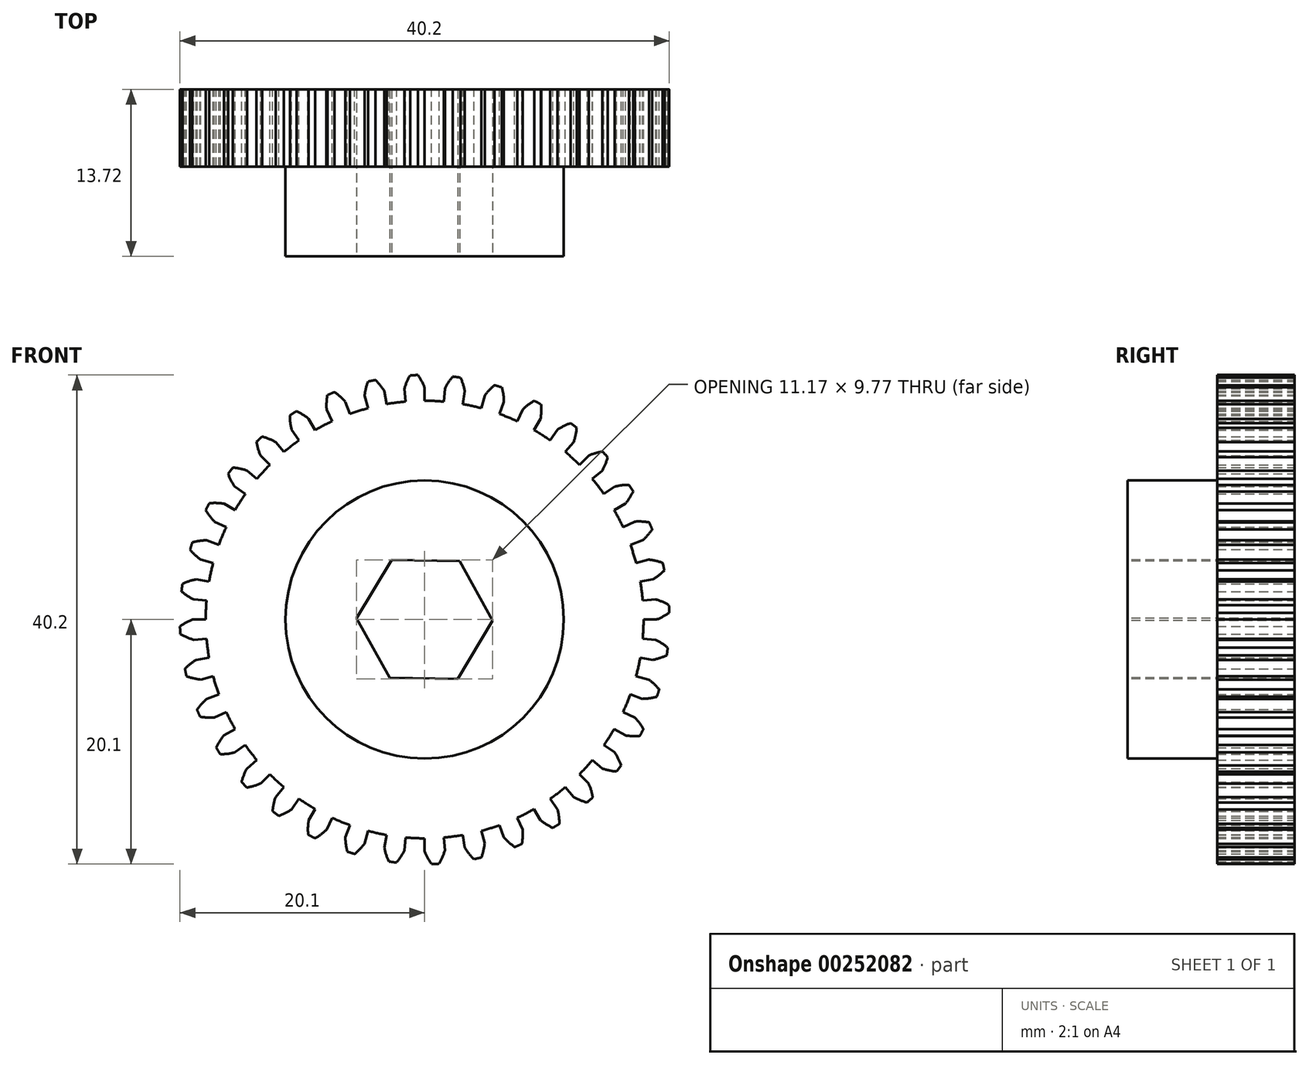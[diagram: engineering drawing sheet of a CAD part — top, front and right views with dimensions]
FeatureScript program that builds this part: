
annotation { "Feature Type Name" : "Feature", "Feature Type Description" : "" }
export const myFeature = defineFeature(function(context is Context, id is Id, definition is map)
    precondition{}
    {
        {
            var Q0;
            Q0=qCreatedBy(makeId("Front.planeOp"),FACE);
            var sketch = newSketch(context, id + "F0", { "sketchPlane" : qUnion([Q0])});
            skArc(sketch, "E0", {"start": v(-0.56, 20.1) * mm, "mid": v(-0.72, 20.1) * mm, "end": v(-0.88, 20.08) * mm});
            skArc(sketch, "E1", {"start": v(-14.73, 10.31) * mm, "mid": v(-15.17, 9.66) * mm, "end": v(-15.57, 9) * mm});
            skLineSegment(sketch, "E2", {"start": v(0, 17.98) * mm, "end": v(0, 19.05) * mm});
            skArc(sketch, "E3.trimOffspring", {"start": v(0, 19.05) * mm, "mid": v(-0.25, 19.6) * mm, "end": v(-0.56, 20.1) * mm});
            skPoint(sketch, "E4.orphan", {"position": v(-2.13, 48.9) * mm});
            skPoint(sketch, "E5.orphan", {"position": v(-2.13, 24.4) * mm});
            skArc(sketch, "E6.MirrorCS", {"start": v(-1.2, 20.07) * mm, "mid": v(-1.03, 20.08) * mm, "end": v(-0.88, 20.08) * mm});
            skArc(sketch, "E7.MirrorCS", {"start": v(-1.66, 18.98) * mm, "mid": v(-1.46, 19.54) * mm, "end": v(-1.2, 20.07) * mm});
            skLineSegment(sketch, "E8.MirrorCS", {"start": v(-1.57, 17.91) * mm, "end": v(-1.66, 18.98) * mm});
            skLineSegment(sketch, "E9.1.0", {"start": v(-4.65, 17.37) * mm, "end": v(-4.93, 18.4) * mm});
            skLineSegment(sketch, "E9.1.1", {"start": v(-3.12, 17.7) * mm, "end": v(-3.3, 18.76) * mm});
            skArc(sketch, "E9.1.2", {"start": v(-4.93, 18.4) * mm, "mid": v(-4.83, 18.99) * mm, "end": v(-4.66, 19.56) * mm});
            skArc(sketch, "E9.1.3", {"start": v(-3.3, 18.76) * mm, "mid": v(-3.65, 19.25) * mm, "end": v(-4.04, 19.7) * mm});
            skArc(sketch, "E9.1.4", {"start": v(-4.04, 19.7) * mm, "mid": v(-4.2, 19.66) * mm, "end": v(-4.35, 19.63) * mm});
            skArc(sketch, "E9.1.5", {"start": v(-4.66, 19.56) * mm, "mid": v(-4.5, 19.6) * mm, "end": v(-4.35, 19.63) * mm});
            skLineSegment(sketch, "E9.2.0", {"start": v(-7.6, 16.3) * mm, "end": v(-8.05, 17.27) * mm});
            skLineSegment(sketch, "E9.2.1", {"start": v(-6.15, 16.9) * mm, "end": v(-6.52, 17.9) * mm});
            skArc(sketch, "E9.2.2", {"start": v(-8.05, 17.27) * mm, "mid": v(-8.05, 17.86) * mm, "end": v(-7.98, 18.45) * mm});
            skArc(sketch, "E9.2.3", {"start": v(-6.52, 17.9) * mm, "mid": v(-6.93, 18.32) * mm, "end": v(-7.4, 18.7) * mm});
            skArc(sketch, "E9.2.4", {"start": v(-7.4, 18.7) * mm, "mid": v(-7.55, 18.63) * mm, "end": v(-7.7, 18.57) * mm});
            skArc(sketch, "E9.2.5", {"start": v(-7.98, 18.45) * mm, "mid": v(-7.84, 18.51) * mm, "end": v(-7.7, 18.57) * mm});
            skLineSegment(sketch, "E9.3.0", {"start": v(-10.31, 14.73) * mm, "end": v(-10.93, 15.6) * mm});
            skLineSegment(sketch, "E9.3.1", {"start": v(-9, 15.57) * mm, "end": v(-9.52, 16.5) * mm});
            skArc(sketch, "E9.3.2", {"start": v(-10.93, 15.6) * mm, "mid": v(-11.03, 16.19) * mm, "end": v(-11.07, 16.78) * mm});
            skArc(sketch, "E9.3.3", {"start": v(-9.52, 16.5) * mm, "mid": v(-10, 16.84) * mm, "end": v(-10.53, 17.12) * mm});
            skArc(sketch, "E9.3.4", {"start": v(-10.53, 17.12) * mm, "mid": v(-10.67, 17.04) * mm, "end": v(-10.8, 16.96) * mm});
            skArc(sketch, "E9.3.5", {"start": v(-11.07, 16.78) * mm, "mid": v(-10.93, 16.87) * mm, "end": v(-10.8, 16.96) * mm});
            skLineSegment(sketch, "E9.4.0", {"start": v(-12.72, 12.72) * mm, "end": v(-13.47, 13.47) * mm});
            skLineSegment(sketch, "E9.4.1", {"start": v(-11.56, 13.78) * mm, "end": v(-12.25, 14.6) * mm});
            skArc(sketch, "E9.4.2", {"start": v(-13.47, 13.47) * mm, "mid": v(-13.68, 14.03) * mm, "end": v(-13.81, 14.6) * mm});
            skArc(sketch, "E9.4.3", {"start": v(-12.25, 14.6) * mm, "mid": v(-12.78, 14.85) * mm, "end": v(-13.35, 15.03) * mm});
            skArc(sketch, "E9.4.4", {"start": v(-13.35, 15.03) * mm, "mid": v(-13.47, 14.93) * mm, "end": v(-13.58, 14.82) * mm});
            skArc(sketch, "E9.4.5", {"start": v(-13.81, 14.6) * mm, "mid": v(-13.7, 14.72) * mm, "end": v(-13.58, 14.82) * mm});
            skLineSegment(sketch, "E9.5.0", {"start": v(-14.73, 10.31) * mm, "end": v(-15.6, 10.93) * mm});
            skLineSegment(sketch, "E9.5.1", {"start": v(-13.78, 11.56) * mm, "end": v(-14.6, 12.25) * mm});
            skArc(sketch, "E9.5.2", {"start": v(-15.6, 10.93) * mm, "mid": v(-15.9, 11.44) * mm, "end": v(-16.14, 11.99) * mm});
            skArc(sketch, "E9.5.3", {"start": v(-14.6, 12.25) * mm, "mid": v(-15.17, 12.4) * mm, "end": v(-15.76, 12.49) * mm});
            skArc(sketch, "E9.5.4", {"start": v(-15.76, 12.49) * mm, "mid": v(-15.85, 12.36) * mm, "end": v(-15.95, 12.24) * mm});
            skArc(sketch, "E9.5.5", {"start": v(-16.14, 11.99) * mm, "mid": v(-16.05, 12.11) * mm, "end": v(-15.95, 12.24) * mm});
            skLineSegment(sketch, "E9.6.0", {"start": v(-16.3, 7.6) * mm, "end": v(-17.27, 8.05) * mm});
            skLineSegment(sketch, "E9.6.1", {"start": v(-15.57, 9) * mm, "end": v(-16.5, 9.53) * mm});
            skArc(sketch, "E9.6.2", {"start": v(-17.27, 8.05) * mm, "mid": v(-17.65, 8.5) * mm, "end": v(-17.98, 9) * mm});
            skArc(sketch, "E9.6.3", {"start": v(-16.5, 9.53) * mm, "mid": v(-17.09, 9.58) * mm, "end": v(-17.68, 9.56) * mm});
            skArc(sketch, "E9.6.4", {"start": v(-17.68, 9.56) * mm, "mid": v(-17.76, 9.42) * mm, "end": v(-17.83, 9.28) * mm});
            skArc(sketch, "E9.6.5", {"start": v(-17.98, 9) * mm, "mid": v(-17.9, 9.14) * mm, "end": v(-17.83, 9.28) * mm});
            skLineSegment(sketch, "E9.7.0", {"start": v(-17.37, 4.65) * mm, "end": v(-18.4, 4.93) * mm});
            skLineSegment(sketch, "E9.7.1", {"start": v(-16.9, 6.15) * mm, "end": v(-17.9, 6.52) * mm});
            skArc(sketch, "E9.7.2", {"start": v(-18.4, 4.93) * mm, "mid": v(-18.86, 5.3) * mm, "end": v(-19.27, 5.74) * mm});
            skArc(sketch, "E9.7.3", {"start": v(-17.9, 6.52) * mm, "mid": v(-18.5, 6.47) * mm, "end": v(-19.08, 6.35) * mm});
            skArc(sketch, "E9.7.4", {"start": v(-19.08, 6.35) * mm, "mid": v(-19.13, 6.2) * mm, "end": v(-19.17, 6.05) * mm});
            skArc(sketch, "E9.7.5", {"start": v(-19.27, 5.74) * mm, "mid": v(-19.22, 5.9) * mm, "end": v(-19.17, 6.05) * mm});
            skLineSegment(sketch, "E9.8.0", {"start": v(-17.91, 1.57) * mm, "end": v(-18.98, 1.66) * mm});
            skLineSegment(sketch, "E9.8.1", {"start": v(-17.7, 3.12) * mm, "end": v(-18.76, 3.3) * mm});
            skArc(sketch, "E9.8.2", {"start": v(-18.98, 1.66) * mm, "mid": v(-19.5, 1.95) * mm, "end": v(-19.97, 2.31) * mm});
            skArc(sketch, "E9.8.3", {"start": v(-18.76, 3.3) * mm, "mid": v(-19.34, 3.16) * mm, "end": v(-19.89, 2.94) * mm});
            skArc(sketch, "E9.8.4", {"start": v(-19.89, 2.94) * mm, "mid": v(-19.91, 2.78) * mm, "end": v(-19.93, 2.62) * mm});
            skArc(sketch, "E9.8.5", {"start": v(-19.97, 2.31) * mm, "mid": v(-19.95, 2.47) * mm, "end": v(-19.93, 2.62) * mm});
            skLineSegment(sketch, "E9.9.0", {"start": v(-17.91, -1.57) * mm, "end": v(-18.98, -1.66) * mm});
            skLineSegment(sketch, "E9.9.1", {"start": v(-17.98, 0) * mm, "end": v(-19.05, 0) * mm});
            skArc(sketch, "E9.9.2", {"start": v(-18.98, -1.66) * mm, "mid": v(-19.54, -1.46) * mm, "end": v(-20.07, -1.2) * mm});
            skArc(sketch, "E9.9.3", {"start": v(-19.05, 0) * mm, "mid": v(-19.6, -0.25) * mm, "end": v(-20.1, -0.56) * mm});
            skArc(sketch, "E9.9.4", {"start": v(-20.1, -0.56) * mm, "mid": v(-20.1, -0.72) * mm, "end": v(-20.08, -0.88) * mm});
            skArc(sketch, "E9.9.5", {"start": v(-20.07, -1.2) * mm, "mid": v(-20.08, -1.03) * mm, "end": v(-20.08, -0.88) * mm});
            skLineSegment(sketch, "E9.10.0", {"start": v(-17.37, -4.65) * mm, "end": v(-18.4, -4.93) * mm});
            skLineSegment(sketch, "E9.10.1", {"start": v(-17.7, -3.12) * mm, "end": v(-18.76, -3.3) * mm});
            skArc(sketch, "E9.10.2", {"start": v(-18.4, -4.93) * mm, "mid": v(-18.99, -4.83) * mm, "end": v(-19.56, -4.66) * mm});
            skArc(sketch, "E9.10.3", {"start": v(-18.76, -3.3) * mm, "mid": v(-19.25, -3.65) * mm, "end": v(-19.7, -4.04) * mm});
            skArc(sketch, "E9.10.4", {"start": v(-19.7, -4.04) * mm, "mid": v(-19.66, -4.2) * mm, "end": v(-19.63, -4.35) * mm});
            skArc(sketch, "E9.10.5", {"start": v(-19.56, -4.66) * mm, "mid": v(-19.6, -4.5) * mm, "end": v(-19.63, -4.35) * mm});
            skLineSegment(sketch, "E9.11.0", {"start": v(-16.3, -7.6) * mm, "end": v(-17.27, -8.05) * mm});
            skLineSegment(sketch, "E9.11.1", {"start": v(-16.9, -6.15) * mm, "end": v(-17.9, -6.52) * mm});
            skArc(sketch, "E9.11.2", {"start": v(-17.27, -8.05) * mm, "mid": v(-17.86, -8.05) * mm, "end": v(-18.45, -7.98) * mm});
            skArc(sketch, "E9.11.3", {"start": v(-17.9, -6.52) * mm, "mid": v(-18.32, -6.93) * mm, "end": v(-18.7, -7.4) * mm});
            skArc(sketch, "E9.11.4", {"start": v(-18.7, -7.4) * mm, "mid": v(-18.63, -7.55) * mm, "end": v(-18.57, -7.7) * mm});
            skArc(sketch, "E9.11.5", {"start": v(-18.45, -7.98) * mm, "mid": v(-18.51, -7.84) * mm, "end": v(-18.57, -7.7) * mm});
            skLineSegment(sketch, "E9.12.0", {"start": v(-14.73, -10.31) * mm, "end": v(-15.6, -10.93) * mm});
            skLineSegment(sketch, "E9.12.1", {"start": v(-15.57, -9) * mm, "end": v(-16.5, -9.52) * mm});
            skArc(sketch, "E9.12.2", {"start": v(-15.6, -10.93) * mm, "mid": v(-16.19, -11.03) * mm, "end": v(-16.78, -11.07) * mm});
            skArc(sketch, "E9.12.3", {"start": v(-16.5, -9.52) * mm, "mid": v(-16.84, -10) * mm, "end": v(-17.12, -10.53) * mm});
            skArc(sketch, "E9.12.4", {"start": v(-17.12, -10.53) * mm, "mid": v(-17.04, -10.67) * mm, "end": v(-16.96, -10.8) * mm});
            skArc(sketch, "E9.12.5", {"start": v(-16.78, -11.07) * mm, "mid": v(-16.87, -10.93) * mm, "end": v(-16.96, -10.8) * mm});
            skLineSegment(sketch, "E9.13.0", {"start": v(-12.72, -12.72) * mm, "end": v(-13.47, -13.47) * mm});
            skLineSegment(sketch, "E9.13.1", {"start": v(-13.78, -11.56) * mm, "end": v(-14.6, -12.25) * mm});
            skArc(sketch, "E9.13.2", {"start": v(-13.47, -13.47) * mm, "mid": v(-14.03, -13.68) * mm, "end": v(-14.6, -13.81) * mm});
            skArc(sketch, "E9.13.3", {"start": v(-14.6, -12.25) * mm, "mid": v(-14.85, -12.78) * mm, "end": v(-15.03, -13.35) * mm});
            skArc(sketch, "E9.13.4", {"start": v(-15.03, -13.35) * mm, "mid": v(-14.93, -13.47) * mm, "end": v(-14.82, -13.58) * mm});
            skArc(sketch, "E9.13.5", {"start": v(-14.6, -13.81) * mm, "mid": v(-14.72, -13.7) * mm, "end": v(-14.82, -13.58) * mm});
            skLineSegment(sketch, "E9.14.0", {"start": v(-10.31, -14.73) * mm, "end": v(-10.93, -15.6) * mm});
            skLineSegment(sketch, "E9.14.1", {"start": v(-11.56, -13.78) * mm, "end": v(-12.25, -14.6) * mm});
            skArc(sketch, "E9.14.2", {"start": v(-10.93, -15.6) * mm, "mid": v(-11.44, -15.9) * mm, "end": v(-11.99, -16.14) * mm});
            skArc(sketch, "E9.14.3", {"start": v(-12.25, -14.6) * mm, "mid": v(-12.4, -15.17) * mm, "end": v(-12.49, -15.76) * mm});
            skArc(sketch, "E9.14.4", {"start": v(-12.49, -15.76) * mm, "mid": v(-12.36, -15.85) * mm, "end": v(-12.24, -15.95) * mm});
            skArc(sketch, "E9.14.5", {"start": v(-11.99, -16.14) * mm, "mid": v(-12.11, -16.05) * mm, "end": v(-12.24, -15.95) * mm});
            skLineSegment(sketch, "E9.15.0", {"start": v(-7.6, -16.3) * mm, "end": v(-8.05, -17.27) * mm});
            skLineSegment(sketch, "E9.15.1", {"start": v(-9, -15.57) * mm, "end": v(-9.53, -16.5) * mm});
            skArc(sketch, "E9.15.2", {"start": v(-8.05, -17.27) * mm, "mid": v(-8.5, -17.65) * mm, "end": v(-9, -17.98) * mm});
            skArc(sketch, "E9.15.3", {"start": v(-9.53, -16.5) * mm, "mid": v(-9.58, -17.09) * mm, "end": v(-9.56, -17.68) * mm});
            skArc(sketch, "E9.15.4", {"start": v(-9.56, -17.68) * mm, "mid": v(-9.42, -17.76) * mm, "end": v(-9.28, -17.83) * mm});
            skArc(sketch, "E9.15.5", {"start": v(-9, -17.98) * mm, "mid": v(-9.14, -17.9) * mm, "end": v(-9.28, -17.83) * mm});
            skLineSegment(sketch, "E9.16.0", {"start": v(-4.65, -17.37) * mm, "end": v(-4.93, -18.4) * mm});
            skLineSegment(sketch, "E9.16.1", {"start": v(-6.15, -16.9) * mm, "end": v(-6.52, -17.9) * mm});
            skArc(sketch, "E9.16.2", {"start": v(-4.93, -18.4) * mm, "mid": v(-5.3, -18.86) * mm, "end": v(-5.74, -19.27) * mm});
            skArc(sketch, "E9.16.3", {"start": v(-6.52, -17.9) * mm, "mid": v(-6.47, -18.5) * mm, "end": v(-6.35, -19.08) * mm});
            skArc(sketch, "E9.16.4", {"start": v(-6.35, -19.08) * mm, "mid": v(-6.2, -19.13) * mm, "end": v(-6.05, -19.17) * mm});
            skArc(sketch, "E9.16.5", {"start": v(-5.74, -19.27) * mm, "mid": v(-5.9, -19.22) * mm, "end": v(-6.05, -19.17) * mm});
            skLineSegment(sketch, "E9.17.0", {"start": v(-1.57, -17.91) * mm, "end": v(-1.66, -18.98) * mm});
            skLineSegment(sketch, "E9.17.1", {"start": v(-3.12, -17.7) * mm, "end": v(-3.3, -18.76) * mm});
            skArc(sketch, "E9.17.2", {"start": v(-1.66, -18.98) * mm, "mid": v(-1.95, -19.5) * mm, "end": v(-2.31, -19.97) * mm});
            skArc(sketch, "E9.17.3", {"start": v(-3.3, -18.76) * mm, "mid": v(-3.16, -19.34) * mm, "end": v(-2.94, -19.89) * mm});
            skArc(sketch, "E9.17.4", {"start": v(-2.94, -19.89) * mm, "mid": v(-2.78, -19.91) * mm, "end": v(-2.62, -19.93) * mm});
            skArc(sketch, "E9.17.5", {"start": v(-2.31, -19.97) * mm, "mid": v(-2.47, -19.95) * mm, "end": v(-2.62, -19.93) * mm});
            skLineSegment(sketch, "E9.18.0", {"start": v(1.57, -17.91) * mm, "end": v(1.66, -18.98) * mm});
            skLineSegment(sketch, "E9.18.1", {"start": v(0, -17.98) * mm, "end": v(0, -19.05) * mm});
            skArc(sketch, "E9.18.2", {"start": v(1.66, -18.98) * mm, "mid": v(1.46, -19.54) * mm, "end": v(1.2, -20.07) * mm});
            skArc(sketch, "E9.18.3", {"start": v(0, -19.05) * mm, "mid": v(0.25, -19.6) * mm, "end": v(0.56, -20.1) * mm});
            skArc(sketch, "E9.18.4", {"start": v(0.56, -20.1) * mm, "mid": v(0.72, -20.1) * mm, "end": v(0.88, -20.08) * mm});
            skArc(sketch, "E9.18.5", {"start": v(1.2, -20.07) * mm, "mid": v(1.03, -20.08) * mm, "end": v(0.88, -20.08) * mm});
            skLineSegment(sketch, "E9.19.0", {"start": v(4.65, -17.37) * mm, "end": v(4.93, -18.4) * mm});
            skLineSegment(sketch, "E9.19.1", {"start": v(3.12, -17.7) * mm, "end": v(3.3, -18.76) * mm});
            skArc(sketch, "E9.19.2", {"start": v(4.93, -18.4) * mm, "mid": v(4.83, -18.99) * mm, "end": v(4.66, -19.56) * mm});
            skArc(sketch, "E9.19.3", {"start": v(3.3, -18.76) * mm, "mid": v(3.65, -19.25) * mm, "end": v(4.04, -19.7) * mm});
            skArc(sketch, "E9.19.4", {"start": v(4.04, -19.7) * mm, "mid": v(4.2, -19.66) * mm, "end": v(4.35, -19.63) * mm});
            skArc(sketch, "E9.19.5", {"start": v(4.66, -19.56) * mm, "mid": v(4.5, -19.6) * mm, "end": v(4.35, -19.63) * mm});
            skLineSegment(sketch, "E9.20.0", {"start": v(7.6, -16.3) * mm, "end": v(8.05, -17.27) * mm});
            skLineSegment(sketch, "E9.20.1", {"start": v(6.15, -16.9) * mm, "end": v(6.52, -17.9) * mm});
            skArc(sketch, "E9.20.2", {"start": v(8.05, -17.27) * mm, "mid": v(8.05, -17.86) * mm, "end": v(7.98, -18.45) * mm});
            skArc(sketch, "E9.20.3", {"start": v(6.52, -17.9) * mm, "mid": v(6.93, -18.32) * mm, "end": v(7.4, -18.7) * mm});
            skArc(sketch, "E9.20.4", {"start": v(7.4, -18.7) * mm, "mid": v(7.55, -18.63) * mm, "end": v(7.7, -18.57) * mm});
            skArc(sketch, "E9.20.5", {"start": v(7.98, -18.45) * mm, "mid": v(7.84, -18.51) * mm, "end": v(7.7, -18.57) * mm});
            skLineSegment(sketch, "E9.21.0", {"start": v(10.31, -14.73) * mm, "end": v(10.93, -15.6) * mm});
            skLineSegment(sketch, "E9.21.1", {"start": v(9, -15.57) * mm, "end": v(9.53, -16.5) * mm});
            skArc(sketch, "E9.21.2", {"start": v(10.93, -15.6) * mm, "mid": v(11.03, -16.19) * mm, "end": v(11.07, -16.78) * mm});
            skArc(sketch, "E9.21.3", {"start": v(9.53, -16.5) * mm, "mid": v(10, -16.84) * mm, "end": v(10.53, -17.12) * mm});
            skArc(sketch, "E9.21.4", {"start": v(10.53, -17.12) * mm, "mid": v(10.67, -17.04) * mm, "end": v(10.8, -16.96) * mm});
            skArc(sketch, "E9.21.5", {"start": v(11.07, -16.78) * mm, "mid": v(10.93, -16.87) * mm, "end": v(10.8, -16.96) * mm});
            skLineSegment(sketch, "E9.22.0", {"start": v(12.72, -12.72) * mm, "end": v(13.47, -13.47) * mm});
            skLineSegment(sketch, "E9.22.1", {"start": v(11.56, -13.78) * mm, "end": v(12.25, -14.6) * mm});
            skArc(sketch, "E9.22.2", {"start": v(13.47, -13.47) * mm, "mid": v(13.68, -14.03) * mm, "end": v(13.81, -14.6) * mm});
            skArc(sketch, "E9.22.3", {"start": v(12.25, -14.6) * mm, "mid": v(12.78, -14.85) * mm, "end": v(13.35, -15.03) * mm});
            skArc(sketch, "E9.22.4", {"start": v(13.35, -15.03) * mm, "mid": v(13.47, -14.93) * mm, "end": v(13.58, -14.82) * mm});
            skArc(sketch, "E9.22.5", {"start": v(13.81, -14.6) * mm, "mid": v(13.7, -14.72) * mm, "end": v(13.58, -14.82) * mm});
            skLineSegment(sketch, "E9.23.0", {"start": v(14.73, -10.31) * mm, "end": v(15.6, -10.93) * mm});
            skLineSegment(sketch, "E9.23.1", {"start": v(13.78, -11.56) * mm, "end": v(14.6, -12.25) * mm});
            skArc(sketch, "E9.23.2", {"start": v(15.6, -10.93) * mm, "mid": v(15.9, -11.44) * mm, "end": v(16.14, -11.99) * mm});
            skArc(sketch, "E9.23.3", {"start": v(14.6, -12.25) * mm, "mid": v(15.17, -12.4) * mm, "end": v(15.76, -12.49) * mm});
            skArc(sketch, "E9.23.4", {"start": v(15.76, -12.49) * mm, "mid": v(15.85, -12.36) * mm, "end": v(15.95, -12.24) * mm});
            skArc(sketch, "E9.23.5", {"start": v(16.14, -11.99) * mm, "mid": v(16.05, -12.11) * mm, "end": v(15.95, -12.24) * mm});
            skLineSegment(sketch, "E9.24.0", {"start": v(16.3, -7.6) * mm, "end": v(17.27, -8.05) * mm});
            skLineSegment(sketch, "E9.24.1", {"start": v(15.57, -9) * mm, "end": v(16.5, -9.53) * mm});
            skArc(sketch, "E9.24.2", {"start": v(17.27, -8.05) * mm, "mid": v(17.65, -8.5) * mm, "end": v(17.98, -9) * mm});
            skArc(sketch, "E9.24.3", {"start": v(16.5, -9.53) * mm, "mid": v(17.09, -9.58) * mm, "end": v(17.68, -9.56) * mm});
            skArc(sketch, "E9.24.4", {"start": v(17.68, -9.56) * mm, "mid": v(17.76, -9.42) * mm, "end": v(17.83, -9.28) * mm});
            skArc(sketch, "E9.24.5", {"start": v(17.98, -9) * mm, "mid": v(17.9, -9.14) * mm, "end": v(17.83, -9.28) * mm});
            skLineSegment(sketch, "E9.25.0", {"start": v(17.37, -4.65) * mm, "end": v(18.4, -4.93) * mm});
            skLineSegment(sketch, "E9.25.1", {"start": v(16.9, -6.15) * mm, "end": v(17.9, -6.52) * mm});
            skArc(sketch, "E9.25.2", {"start": v(18.4, -4.93) * mm, "mid": v(18.86, -5.3) * mm, "end": v(19.27, -5.74) * mm});
            skArc(sketch, "E9.25.3", {"start": v(17.9, -6.52) * mm, "mid": v(18.5, -6.47) * mm, "end": v(19.08, -6.35) * mm});
            skArc(sketch, "E9.25.4", {"start": v(19.08, -6.35) * mm, "mid": v(19.13, -6.2) * mm, "end": v(19.17, -6.05) * mm});
            skArc(sketch, "E9.25.5", {"start": v(19.27, -5.74) * mm, "mid": v(19.22, -5.9) * mm, "end": v(19.17, -6.05) * mm});
            skLineSegment(sketch, "E9.26.0", {"start": v(17.91, -1.57) * mm, "end": v(18.98, -1.66) * mm});
            skLineSegment(sketch, "E9.26.1", {"start": v(17.7, -3.12) * mm, "end": v(18.76, -3.3) * mm});
            skArc(sketch, "E9.26.2", {"start": v(18.98, -1.66) * mm, "mid": v(19.5, -1.95) * mm, "end": v(19.97, -2.31) * mm});
            skArc(sketch, "E9.26.3", {"start": v(18.76, -3.3) * mm, "mid": v(19.34, -3.16) * mm, "end": v(19.89, -2.94) * mm});
            skArc(sketch, "E9.26.4", {"start": v(19.89, -2.94) * mm, "mid": v(19.91, -2.78) * mm, "end": v(19.93, -2.62) * mm});
            skArc(sketch, "E9.26.5", {"start": v(19.97, -2.31) * mm, "mid": v(19.95, -2.47) * mm, "end": v(19.93, -2.62) * mm});
            skLineSegment(sketch, "E9.27.0", {"start": v(17.91, 1.57) * mm, "end": v(18.98, 1.66) * mm});
            skLineSegment(sketch, "E9.27.1", {"start": v(17.98, 0) * mm, "end": v(19.05, 0) * mm});
            skArc(sketch, "E9.27.2", {"start": v(18.98, 1.66) * mm, "mid": v(19.54, 1.46) * mm, "end": v(20.07, 1.2) * mm});
            skArc(sketch, "E9.27.3", {"start": v(19.05, 0) * mm, "mid": v(19.6, 0.25) * mm, "end": v(20.1, 0.56) * mm});
            skArc(sketch, "E9.27.4", {"start": v(20.1, 0.56) * mm, "mid": v(20.1, 0.72) * mm, "end": v(20.08, 0.88) * mm});
            skArc(sketch, "E9.27.5", {"start": v(20.07, 1.2) * mm, "mid": v(20.08, 1.03) * mm, "end": v(20.08, 0.88) * mm});
            skLineSegment(sketch, "E9.28.0", {"start": v(17.37, 4.65) * mm, "end": v(18.4, 4.93) * mm});
            skLineSegment(sketch, "E9.28.1", {"start": v(17.7, 3.12) * mm, "end": v(18.76, 3.3) * mm});
            skArc(sketch, "E9.28.2", {"start": v(18.4, 4.93) * mm, "mid": v(18.99, 4.83) * mm, "end": v(19.56, 4.66) * mm});
            skArc(sketch, "E9.28.3", {"start": v(18.76, 3.3) * mm, "mid": v(19.25, 3.65) * mm, "end": v(19.7, 4.04) * mm});
            skArc(sketch, "E9.28.4", {"start": v(19.7, 4.04) * mm, "mid": v(19.66, 4.2) * mm, "end": v(19.63, 4.35) * mm});
            skArc(sketch, "E9.28.5", {"start": v(19.56, 4.66) * mm, "mid": v(19.6, 4.5) * mm, "end": v(19.63, 4.35) * mm});
            skLineSegment(sketch, "E9.29.0", {"start": v(16.3, 7.6) * mm, "end": v(17.27, 8.05) * mm});
            skLineSegment(sketch, "E9.29.1", {"start": v(16.9, 6.15) * mm, "end": v(17.9, 6.52) * mm});
            skArc(sketch, "E9.29.2", {"start": v(17.27, 8.05) * mm, "mid": v(17.86, 8.05) * mm, "end": v(18.45, 7.98) * mm});
            skArc(sketch, "E9.29.3", {"start": v(17.9, 6.52) * mm, "mid": v(18.32, 6.93) * mm, "end": v(18.7, 7.4) * mm});
            skArc(sketch, "E9.29.4", {"start": v(18.7, 7.4) * mm, "mid": v(18.63, 7.55) * mm, "end": v(18.57, 7.7) * mm});
            skArc(sketch, "E9.29.5", {"start": v(18.45, 7.98) * mm, "mid": v(18.51, 7.84) * mm, "end": v(18.57, 7.7) * mm});
            skLineSegment(sketch, "E9.30.0", {"start": v(14.73, 10.31) * mm, "end": v(15.6, 10.93) * mm});
            skLineSegment(sketch, "E9.30.1", {"start": v(15.57, 9) * mm, "end": v(16.5, 9.52) * mm});
            skArc(sketch, "E9.30.2", {"start": v(15.6, 10.93) * mm, "mid": v(16.19, 11.03) * mm, "end": v(16.78, 11.07) * mm});
            skArc(sketch, "E9.30.3", {"start": v(16.5, 9.52) * mm, "mid": v(16.84, 10) * mm, "end": v(17.12, 10.53) * mm});
            skArc(sketch, "E9.30.4", {"start": v(17.12, 10.53) * mm, "mid": v(17.04, 10.67) * mm, "end": v(16.96, 10.8) * mm});
            skArc(sketch, "E9.30.5", {"start": v(16.78, 11.07) * mm, "mid": v(16.87, 10.93) * mm, "end": v(16.96, 10.8) * mm});
            skLineSegment(sketch, "E9.31.0", {"start": v(12.72, 12.72) * mm, "end": v(13.47, 13.47) * mm});
            skLineSegment(sketch, "E9.31.1", {"start": v(13.78, 11.56) * mm, "end": v(14.6, 12.25) * mm});
            skArc(sketch, "E9.31.2", {"start": v(13.47, 13.47) * mm, "mid": v(14.03, 13.68) * mm, "end": v(14.6, 13.81) * mm});
            skArc(sketch, "E9.31.3", {"start": v(14.6, 12.25) * mm, "mid": v(14.85, 12.78) * mm, "end": v(15.03, 13.35) * mm});
            skArc(sketch, "E9.31.4", {"start": v(15.03, 13.35) * mm, "mid": v(14.93, 13.47) * mm, "end": v(14.82, 13.58) * mm});
            skArc(sketch, "E9.31.5", {"start": v(14.6, 13.81) * mm, "mid": v(14.72, 13.7) * mm, "end": v(14.82, 13.58) * mm});
            skLineSegment(sketch, "E9.32.0", {"start": v(10.31, 14.73) * mm, "end": v(10.93, 15.6) * mm});
            skLineSegment(sketch, "E9.32.1", {"start": v(11.56, 13.78) * mm, "end": v(12.25, 14.6) * mm});
            skArc(sketch, "E9.32.2", {"start": v(10.93, 15.6) * mm, "mid": v(11.44, 15.9) * mm, "end": v(11.99, 16.14) * mm});
            skArc(sketch, "E9.32.3", {"start": v(12.25, 14.6) * mm, "mid": v(12.4, 15.17) * mm, "end": v(12.49, 15.76) * mm});
            skArc(sketch, "E9.32.4", {"start": v(12.49, 15.76) * mm, "mid": v(12.36, 15.85) * mm, "end": v(12.24, 15.95) * mm});
            skArc(sketch, "E9.32.5", {"start": v(11.99, 16.14) * mm, "mid": v(12.11, 16.05) * mm, "end": v(12.24, 15.95) * mm});
            skLineSegment(sketch, "E9.33.0", {"start": v(7.6, 16.3) * mm, "end": v(8.05, 17.27) * mm});
            skLineSegment(sketch, "E9.33.1", {"start": v(9, 15.57) * mm, "end": v(9.52, 16.5) * mm});
            skArc(sketch, "E9.33.2", {"start": v(8.05, 17.27) * mm, "mid": v(8.5, 17.65) * mm, "end": v(9, 17.98) * mm});
            skArc(sketch, "E9.33.3", {"start": v(9.52, 16.5) * mm, "mid": v(9.58, 17.09) * mm, "end": v(9.56, 17.68) * mm});
            skArc(sketch, "E9.33.4", {"start": v(9.56, 17.68) * mm, "mid": v(9.42, 17.76) * mm, "end": v(9.28, 17.83) * mm});
            skArc(sketch, "E9.33.5", {"start": v(9, 17.98) * mm, "mid": v(9.14, 17.9) * mm, "end": v(9.28, 17.83) * mm});
            skLineSegment(sketch, "E9.34.0", {"start": v(4.65, 17.37) * mm, "end": v(4.93, 18.4) * mm});
            skLineSegment(sketch, "E9.34.1", {"start": v(6.15, 16.9) * mm, "end": v(6.52, 17.9) * mm});
            skArc(sketch, "E9.34.2", {"start": v(4.93, 18.4) * mm, "mid": v(5.3, 18.86) * mm, "end": v(5.74, 19.27) * mm});
            skArc(sketch, "E9.34.3", {"start": v(6.52, 17.9) * mm, "mid": v(6.47, 18.5) * mm, "end": v(6.35, 19.08) * mm});
            skArc(sketch, "E9.34.4", {"start": v(6.35, 19.08) * mm, "mid": v(6.2, 19.13) * mm, "end": v(6.05, 19.17) * mm});
            skArc(sketch, "E9.34.5", {"start": v(5.74, 19.27) * mm, "mid": v(5.9, 19.22) * mm, "end": v(6.05, 19.17) * mm});
            skLineSegment(sketch, "E9.35.0", {"start": v(1.57, 17.91) * mm, "end": v(1.66, 18.98) * mm});
            skLineSegment(sketch, "E9.35.1", {"start": v(3.12, 17.7) * mm, "end": v(3.3, 18.76) * mm});
            skArc(sketch, "E9.35.2", {"start": v(1.66, 18.98) * mm, "mid": v(1.95, 19.5) * mm, "end": v(2.31, 19.97) * mm});
            skArc(sketch, "E9.35.3", {"start": v(3.3, 18.76) * mm, "mid": v(3.16, 19.34) * mm, "end": v(2.94, 19.89) * mm});
            skArc(sketch, "E9.35.4", {"start": v(2.94, 19.89) * mm, "mid": v(2.78, 19.91) * mm, "end": v(2.62, 19.93) * mm});
            skArc(sketch, "E9.35.5", {"start": v(2.31, 19.97) * mm, "mid": v(2.47, 19.95) * mm, "end": v(2.62, 19.93) * mm});
            skArc(sketch, "E10.trimOffspring", {"start": v(-12.72, 12.72) * mm, "mid": v(-13.26, 12.15) * mm, "end": v(-13.78, 11.56) * mm});
            skArc(sketch, "E11.trimOffspring", {"start": v(-10.31, 14.73) * mm, "mid": v(-10.95, 14.27) * mm, "end": v(-11.56, 13.78) * mm});
            skArc(sketch, "E12.trimOffspring", {"start": v(-7.6, 16.3) * mm, "mid": v(-8.3, 15.95) * mm, "end": v(-9, 15.57) * mm});
            skArc(sketch, "E13.trimOffspring", {"start": v(-4.65, 17.37) * mm, "mid": v(-5.4, 17.15) * mm, "end": v(-6.15, 16.9) * mm});
            skArc(sketch, "E14.trimOffspring", {"start": v(-1.57, 17.91) * mm, "mid": v(-2.35, 17.83) * mm, "end": v(-3.12, 17.7) * mm});
            skArc(sketch, "E15.trimOffspring", {"start": v(1.57, 17.91) * mm, "mid": v(0.78, 17.97) * mm, "end": v(0, 17.98) * mm});
            skArc(sketch, "E16.trimOffspring", {"start": v(4.65, 17.37) * mm, "mid": v(3.9, 17.56) * mm, "end": v(3.12, 17.7) * mm});
            skArc(sketch, "E17.trimOffspring", {"start": v(7.6, 16.3) * mm, "mid": v(6.88, 16.61) * mm, "end": v(6.15, 16.9) * mm});
            skArc(sketch, "E18.trimOffspring", {"start": v(10.31, 14.73) * mm, "mid": v(9.66, 15.17) * mm, "end": v(9, 15.57) * mm});
            skArc(sketch, "E19.trimOffspring", {"start": v(12.72, 12.72) * mm, "mid": v(12.15, 13.26) * mm, "end": v(11.56, 13.78) * mm});
            skArc(sketch, "E20.trimOffspring", {"start": v(14.73, 10.31) * mm, "mid": v(14.27, 10.95) * mm, "end": v(13.78, 11.56) * mm});
            skArc(sketch, "E21.trimOffspring", {"start": v(16.3, 7.6) * mm, "mid": v(15.95, 8.3) * mm, "end": v(15.57, 9) * mm});
            skArc(sketch, "E22.trimOffspring", {"start": v(17.37, 4.65) * mm, "mid": v(17.15, 5.4) * mm, "end": v(16.9, 6.15) * mm});
            skArc(sketch, "E23.trimOffspring", {"start": v(17.91, 1.57) * mm, "mid": v(17.83, 2.35) * mm, "end": v(17.7, 3.12) * mm});
            skArc(sketch, "E24.trimOffspring", {"start": v(17.91, -1.57) * mm, "mid": v(17.97, -0.78) * mm, "end": v(17.98, 0) * mm});
            skArc(sketch, "E25.trimOffspring", {"start": v(17.37, -4.65) * mm, "mid": v(17.56, -3.9) * mm, "end": v(17.7, -3.12) * mm});
            skArc(sketch, "E26.trimOffspring", {"start": v(16.3, -7.6) * mm, "mid": v(16.61, -6.88) * mm, "end": v(16.9, -6.15) * mm});
            skArc(sketch, "E27.trimOffspring", {"start": v(14.73, -10.31) * mm, "mid": v(15.17, -9.66) * mm, "end": v(15.57, -9) * mm});
            skArc(sketch, "E28.trimOffspring", {"start": v(12.72, -12.72) * mm, "mid": v(13.26, -12.15) * mm, "end": v(13.78, -11.56) * mm});
            skArc(sketch, "E29.trimOffspring", {"start": v(10.31, -14.73) * mm, "mid": v(10.95, -14.27) * mm, "end": v(11.56, -13.78) * mm});
            skArc(sketch, "E30.trimOffspring", {"start": v(7.6, -16.3) * mm, "mid": v(8.3, -15.95) * mm, "end": v(9, -15.57) * mm});
            skArc(sketch, "E31.trimOffspring", {"start": v(4.65, -17.37) * mm, "mid": v(5.4, -17.15) * mm, "end": v(6.15, -16.9) * mm});
            skArc(sketch, "E32.trimOffspring", {"start": v(1.57, -17.91) * mm, "mid": v(2.35, -17.83) * mm, "end": v(3.12, -17.7) * mm});
            skArc(sketch, "E33.trimOffspring", {"start": v(-1.57, -17.91) * mm, "mid": v(-0.78, -17.97) * mm, "end": v(0, -17.98) * mm});
            skArc(sketch, "E34.trimOffspring", {"start": v(-4.65, -17.37) * mm, "mid": v(-3.9, -17.56) * mm, "end": v(-3.12, -17.7) * mm});
            skArc(sketch, "E35.trimOffspring", {"start": v(-7.6, -16.3) * mm, "mid": v(-6.88, -16.61) * mm, "end": v(-6.15, -16.9) * mm});
            skArc(sketch, "E36.trimOffspring", {"start": v(-10.31, -14.73) * mm, "mid": v(-9.66, -15.17) * mm, "end": v(-9, -15.57) * mm});
            skArc(sketch, "E37.trimOffspring", {"start": v(-12.72, -12.72) * mm, "mid": v(-12.15, -13.26) * mm, "end": v(-11.56, -13.78) * mm});
            skArc(sketch, "E38.trimOffspring", {"start": v(-14.73, -10.31) * mm, "mid": v(-14.27, -10.95) * mm, "end": v(-13.78, -11.56) * mm});
            skArc(sketch, "E39.trimOffspring", {"start": v(-16.3, -7.6) * mm, "mid": v(-15.95, -8.3) * mm, "end": v(-15.57, -9) * mm});
            skArc(sketch, "E40.trimOffspring", {"start": v(-17.37, -4.65) * mm, "mid": v(-17.15, -5.4) * mm, "end": v(-16.9, -6.15) * mm});
            skArc(sketch, "E41.trimOffspring", {"start": v(-17.91, -1.57) * mm, "mid": v(-17.83, -2.35) * mm, "end": v(-17.7, -3.12) * mm});
            skArc(sketch, "E42.trimOffspring", {"start": v(-17.91, 1.57) * mm, "mid": v(-17.97, 0.78) * mm, "end": v(-17.98, 0) * mm});
            skArc(sketch, "E43.trimOffspring", {"start": v(-17.37, 4.65) * mm, "mid": v(-17.56, 3.9) * mm, "end": v(-17.7, 3.12) * mm});
            skArc(sketch, "E44.trimOffspring", {"start": v(-16.3, 7.6) * mm, "mid": v(-16.61, 6.88) * mm, "end": v(-16.9, 6.15) * mm});
            skSolve(sketch);
        }
        {
            var Q0;
            Q0=makeQuery(id+"F0.imprint","IMPRINT",FACE,{"disambiguationData":[TD([[makeQuery(id+"F0.imprint","IMPRINT",EDGE,{"derivedFrom":sQuery(id+"F0.wireOp",EDGE,"E0")}),1.0]])]});
            extrude(context, id + "F1", {"entities" : qUnion([Q0]), "depth" : 6.35 * mm});
        }
        {
            var Q0;
            Q0=makeQuery(id+"F1.opExtrude","CAP_FACE",FACE,{"disambiguationData":[OSD([sQuery(id+"F0.wireOp",EDGE,"E0"),sQuery(id+"F0.wireOp",EDGE,"E1"),sQuery(id+"F0.wireOp",EDGE,"E2"),sQuery(id+"F0.wireOp",EDGE,"E3.trimOffspring"),sQuery(id+"F0.wireOp",EDGE,"E6.MirrorCS"),sQuery(id+"F0.wireOp",EDGE,"E7.MirrorCS"),sQuery(id+"F0.wireOp",EDGE,"E8.MirrorCS"),sQuery(id+"F0.wireOp",EDGE,"E9.1.0"),sQuery(id+"F0.wireOp",EDGE,"E9.1.1"),sQuery(id+"F0.wireOp",EDGE,"E9.1.2"),sQuery(id+"F0.wireOp",EDGE,"E9.1.3"),sQuery(id+"F0.wireOp",EDGE,"E9.1.4"),sQuery(id+"F0.wireOp",EDGE,"E9.1.5"),sQuery(id+"F0.wireOp",EDGE,"E9.2.0"),sQuery(id+"F0.wireOp",EDGE,"E9.2.1"),sQuery(id+"F0.wireOp",EDGE,"E9.2.2"),sQuery(id+"F0.wireOp",EDGE,"E9.2.3"),sQuery(id+"F0.wireOp",EDGE,"E9.2.4"),sQuery(id+"F0.wireOp",EDGE,"E9.2.5"),sQuery(id+"F0.wireOp",EDGE,"E9.3.0"),sQuery(id+"F0.wireOp",EDGE,"E9.3.1"),sQuery(id+"F0.wireOp",EDGE,"E9.3.2"),sQuery(id+"F0.wireOp",EDGE,"E9.3.3"),sQuery(id+"F0.wireOp",EDGE,"E9.3.4"),sQuery(id+"F0.wireOp",EDGE,"E9.3.5"),sQuery(id+"F0.wireOp",EDGE,"E9.4.0"),sQuery(id+"F0.wireOp",EDGE,"E9.4.1"),sQuery(id+"F0.wireOp",EDGE,"E9.4.2"),sQuery(id+"F0.wireOp",EDGE,"E9.4.3"),sQuery(id+"F0.wireOp",EDGE,"E9.4.4"),sQuery(id+"F0.wireOp",EDGE,"E9.4.5"),sQuery(id+"F0.wireOp",EDGE,"E9.5.0"),sQuery(id+"F0.wireOp",EDGE,"E9.5.1"),sQuery(id+"F0.wireOp",EDGE,"E9.5.2"),sQuery(id+"F0.wireOp",EDGE,"E9.5.3"),sQuery(id+"F0.wireOp",EDGE,"E9.5.4"),sQuery(id+"F0.wireOp",EDGE,"E9.5.5"),sQuery(id+"F0.wireOp",EDGE,"E9.6.0"),sQuery(id+"F0.wireOp",EDGE,"E9.6.1"),sQuery(id+"F0.wireOp",EDGE,"E9.6.2"),sQuery(id+"F0.wireOp",EDGE,"E9.6.3"),sQuery(id+"F0.wireOp",EDGE,"E9.6.4"),sQuery(id+"F0.wireOp",EDGE,"E9.6.5"),sQuery(id+"F0.wireOp",EDGE,"E9.7.0"),sQuery(id+"F0.wireOp",EDGE,"E9.7.1"),sQuery(id+"F0.wireOp",EDGE,"E9.7.2"),sQuery(id+"F0.wireOp",EDGE,"E9.7.3"),sQuery(id+"F0.wireOp",EDGE,"E9.7.4"),sQuery(id+"F0.wireOp",EDGE,"E9.7.5"),sQuery(id+"F0.wireOp",EDGE,"E9.8.0"),sQuery(id+"F0.wireOp",EDGE,"E9.8.1"),sQuery(id+"F0.wireOp",EDGE,"E9.8.2"),sQuery(id+"F0.wireOp",EDGE,"E9.8.3"),sQuery(id+"F0.wireOp",EDGE,"E9.8.4"),sQuery(id+"F0.wireOp",EDGE,"E9.8.5"),sQuery(id+"F0.wireOp",EDGE,"E9.9.0"),sQuery(id+"F0.wireOp",EDGE,"E9.9.1"),sQuery(id+"F0.wireOp",EDGE,"E9.9.2"),sQuery(id+"F0.wireOp",EDGE,"E9.9.3"),sQuery(id+"F0.wireOp",EDGE,"E9.9.4"),sQuery(id+"F0.wireOp",EDGE,"E9.9.5"),sQuery(id+"F0.wireOp",EDGE,"E9.10.0"),sQuery(id+"F0.wireOp",EDGE,"E9.10.1"),sQuery(id+"F0.wireOp",EDGE,"E9.10.2"),sQuery(id+"F0.wireOp",EDGE,"E9.10.3"),sQuery(id+"F0.wireOp",EDGE,"E9.10.4"),sQuery(id+"F0.wireOp",EDGE,"E9.10.5"),sQuery(id+"F0.wireOp",EDGE,"E9.11.0"),sQuery(id+"F0.wireOp",EDGE,"E9.11.1"),sQuery(id+"F0.wireOp",EDGE,"E9.11.2"),sQuery(id+"F0.wireOp",EDGE,"E9.11.3"),sQuery(id+"F0.wireOp",EDGE,"E9.11.4"),sQuery(id+"F0.wireOp",EDGE,"E9.11.5"),sQuery(id+"F0.wireOp",EDGE,"E9.12.0"),sQuery(id+"F0.wireOp",EDGE,"E9.12.1"),sQuery(id+"F0.wireOp",EDGE,"E9.12.2"),sQuery(id+"F0.wireOp",EDGE,"E9.12.3"),sQuery(id+"F0.wireOp",EDGE,"E9.12.4"),sQuery(id+"F0.wireOp",EDGE,"E9.12.5"),sQuery(id+"F0.wireOp",EDGE,"E9.13.0"),sQuery(id+"F0.wireOp",EDGE,"E9.13.1"),sQuery(id+"F0.wireOp",EDGE,"E9.13.2"),sQuery(id+"F0.wireOp",EDGE,"E9.13.3"),sQuery(id+"F0.wireOp",EDGE,"E9.13.4"),sQuery(id+"F0.wireOp",EDGE,"E9.13.5"),sQuery(id+"F0.wireOp",EDGE,"E9.14.0"),sQuery(id+"F0.wireOp",EDGE,"E9.14.1"),sQuery(id+"F0.wireOp",EDGE,"E9.14.2"),sQuery(id+"F0.wireOp",EDGE,"E9.14.3"),sQuery(id+"F0.wireOp",EDGE,"E9.14.4"),sQuery(id+"F0.wireOp",EDGE,"E9.14.5"),sQuery(id+"F0.wireOp",EDGE,"E9.15.0"),sQuery(id+"F0.wireOp",EDGE,"E9.15.1"),sQuery(id+"F0.wireOp",EDGE,"E9.15.2"),sQuery(id+"F0.wireOp",EDGE,"E9.15.3"),sQuery(id+"F0.wireOp",EDGE,"E9.15.4"),sQuery(id+"F0.wireOp",EDGE,"E9.15.5"),sQuery(id+"F0.wireOp",EDGE,"E9.16.0"),sQuery(id+"F0.wireOp",EDGE,"E9.16.1"),sQuery(id+"F0.wireOp",EDGE,"E9.16.2"),sQuery(id+"F0.wireOp",EDGE,"E9.16.3"),sQuery(id+"F0.wireOp",EDGE,"E9.16.4"),sQuery(id+"F0.wireOp",EDGE,"E9.16.5"),sQuery(id+"F0.wireOp",EDGE,"E9.17.0"),sQuery(id+"F0.wireOp",EDGE,"E9.17.1"),sQuery(id+"F0.wireOp",EDGE,"E9.17.2"),sQuery(id+"F0.wireOp",EDGE,"E9.17.3"),sQuery(id+"F0.wireOp",EDGE,"E9.17.4"),sQuery(id+"F0.wireOp",EDGE,"E9.17.5"),sQuery(id+"F0.wireOp",EDGE,"E9.18.0"),sQuery(id+"F0.wireOp",EDGE,"E9.18.1"),sQuery(id+"F0.wireOp",EDGE,"E9.18.2"),sQuery(id+"F0.wireOp",EDGE,"E9.18.3"),sQuery(id+"F0.wireOp",EDGE,"E9.18.4"),sQuery(id+"F0.wireOp",EDGE,"E9.18.5"),sQuery(id+"F0.wireOp",EDGE,"E9.19.0"),sQuery(id+"F0.wireOp",EDGE,"E9.19.1"),sQuery(id+"F0.wireOp",EDGE,"E9.19.2"),sQuery(id+"F0.wireOp",EDGE,"E9.19.3"),sQuery(id+"F0.wireOp",EDGE,"E9.19.4"),sQuery(id+"F0.wireOp",EDGE,"E9.19.5"),sQuery(id+"F0.wireOp",EDGE,"E9.20.0"),sQuery(id+"F0.wireOp",EDGE,"E9.20.1"),sQuery(id+"F0.wireOp",EDGE,"E9.20.2"),sQuery(id+"F0.wireOp",EDGE,"E9.20.3"),sQuery(id+"F0.wireOp",EDGE,"E9.20.4"),sQuery(id+"F0.wireOp",EDGE,"E9.20.5"),sQuery(id+"F0.wireOp",EDGE,"E9.21.0"),sQuery(id+"F0.wireOp",EDGE,"E9.21.1"),sQuery(id+"F0.wireOp",EDGE,"E9.21.2"),sQuery(id+"F0.wireOp",EDGE,"E9.21.3"),sQuery(id+"F0.wireOp",EDGE,"E9.21.4"),sQuery(id+"F0.wireOp",EDGE,"E9.21.5"),sQuery(id+"F0.wireOp",EDGE,"E9.22.0"),sQuery(id+"F0.wireOp",EDGE,"E9.22.1"),sQuery(id+"F0.wireOp",EDGE,"E9.22.2"),sQuery(id+"F0.wireOp",EDGE,"E9.22.3"),sQuery(id+"F0.wireOp",EDGE,"E9.22.4"),sQuery(id+"F0.wireOp",EDGE,"E9.22.5"),sQuery(id+"F0.wireOp",EDGE,"E9.23.0"),sQuery(id+"F0.wireOp",EDGE,"E9.23.1"),sQuery(id+"F0.wireOp",EDGE,"E9.23.2"),sQuery(id+"F0.wireOp",EDGE,"E9.23.3"),sQuery(id+"F0.wireOp",EDGE,"E9.23.4"),sQuery(id+"F0.wireOp",EDGE,"E9.23.5"),sQuery(id+"F0.wireOp",EDGE,"E9.24.0"),sQuery(id+"F0.wireOp",EDGE,"E9.24.1"),sQuery(id+"F0.wireOp",EDGE,"E9.24.2"),sQuery(id+"F0.wireOp",EDGE,"E9.24.3"),sQuery(id+"F0.wireOp",EDGE,"E9.24.4"),sQuery(id+"F0.wireOp",EDGE,"E9.24.5"),sQuery(id+"F0.wireOp",EDGE,"E9.25.0"),sQuery(id+"F0.wireOp",EDGE,"E9.25.1"),sQuery(id+"F0.wireOp",EDGE,"E9.25.2"),sQuery(id+"F0.wireOp",EDGE,"E9.25.3"),sQuery(id+"F0.wireOp",EDGE,"E9.25.4"),sQuery(id+"F0.wireOp",EDGE,"E9.25.5"),sQuery(id+"F0.wireOp",EDGE,"E9.26.0"),sQuery(id+"F0.wireOp",EDGE,"E9.26.1"),sQuery(id+"F0.wireOp",EDGE,"E9.26.2"),sQuery(id+"F0.wireOp",EDGE,"E9.26.3"),sQuery(id+"F0.wireOp",EDGE,"E9.26.4"),sQuery(id+"F0.wireOp",EDGE,"E9.26.5"),sQuery(id+"F0.wireOp",EDGE,"E9.27.0"),sQuery(id+"F0.wireOp",EDGE,"E9.27.1"),sQuery(id+"F0.wireOp",EDGE,"E9.27.2"),sQuery(id+"F0.wireOp",EDGE,"E9.27.3"),sQuery(id+"F0.wireOp",EDGE,"E9.27.4"),sQuery(id+"F0.wireOp",EDGE,"E9.27.5"),sQuery(id+"F0.wireOp",EDGE,"E9.28.0"),sQuery(id+"F0.wireOp",EDGE,"E9.28.1"),sQuery(id+"F0.wireOp",EDGE,"E9.28.2"),sQuery(id+"F0.wireOp",EDGE,"E9.28.3"),sQuery(id+"F0.wireOp",EDGE,"E9.28.4"),sQuery(id+"F0.wireOp",EDGE,"E9.28.5"),sQuery(id+"F0.wireOp",EDGE,"E9.29.0"),sQuery(id+"F0.wireOp",EDGE,"E9.29.1"),sQuery(id+"F0.wireOp",EDGE,"E9.29.2"),sQuery(id+"F0.wireOp",EDGE,"E9.29.3"),sQuery(id+"F0.wireOp",EDGE,"E9.29.4"),sQuery(id+"F0.wireOp",EDGE,"E9.29.5"),sQuery(id+"F0.wireOp",EDGE,"E9.30.0"),sQuery(id+"F0.wireOp",EDGE,"E9.30.1"),sQuery(id+"F0.wireOp",EDGE,"E9.30.2"),sQuery(id+"F0.wireOp",EDGE,"E9.30.3"),sQuery(id+"F0.wireOp",EDGE,"E9.30.4"),sQuery(id+"F0.wireOp",EDGE,"E9.30.5"),sQuery(id+"F0.wireOp",EDGE,"E9.31.0"),sQuery(id+"F0.wireOp",EDGE,"E9.31.1"),sQuery(id+"F0.wireOp",EDGE,"E9.31.2"),sQuery(id+"F0.wireOp",EDGE,"E9.31.3"),sQuery(id+"F0.wireOp",EDGE,"E9.31.4"),sQuery(id+"F0.wireOp",EDGE,"E9.31.5"),sQuery(id+"F0.wireOp",EDGE,"E9.32.0"),sQuery(id+"F0.wireOp",EDGE,"E9.32.1"),sQuery(id+"F0.wireOp",EDGE,"E9.32.2"),sQuery(id+"F0.wireOp",EDGE,"E9.32.3"),sQuery(id+"F0.wireOp",EDGE,"E9.32.4"),sQuery(id+"F0.wireOp",EDGE,"E9.32.5"),sQuery(id+"F0.wireOp",EDGE,"E9.33.0"),sQuery(id+"F0.wireOp",EDGE,"E9.33.1"),sQuery(id+"F0.wireOp",EDGE,"E9.33.2"),sQuery(id+"F0.wireOp",EDGE,"E9.33.3"),sQuery(id+"F0.wireOp",EDGE,"E9.33.4"),sQuery(id+"F0.wireOp",EDGE,"E9.33.5"),sQuery(id+"F0.wireOp",EDGE,"E9.34.0"),sQuery(id+"F0.wireOp",EDGE,"E9.34.1"),sQuery(id+"F0.wireOp",EDGE,"E9.34.2"),sQuery(id+"F0.wireOp",EDGE,"E9.34.3"),sQuery(id+"F0.wireOp",EDGE,"E9.34.4"),sQuery(id+"F0.wireOp",EDGE,"E9.34.5"),sQuery(id+"F0.wireOp",EDGE,"E9.35.0"),sQuery(id+"F0.wireOp",EDGE,"E9.35.1"),sQuery(id+"F0.wireOp",EDGE,"E9.35.2"),sQuery(id+"F0.wireOp",EDGE,"E9.35.3"),sQuery(id+"F0.wireOp",EDGE,"E9.35.4"),sQuery(id+"F0.wireOp",EDGE,"E9.35.5"),sQuery(id+"F0.wireOp",EDGE,"E10.trimOffspring"),sQuery(id+"F0.wireOp",EDGE,"E11.trimOffspring"),sQuery(id+"F0.wireOp",EDGE,"E12.trimOffspring"),sQuery(id+"F0.wireOp",EDGE,"E13.trimOffspring"),sQuery(id+"F0.wireOp",EDGE,"E14.trimOffspring"),sQuery(id+"F0.wireOp",EDGE,"E15.trimOffspring"),sQuery(id+"F0.wireOp",EDGE,"E16.trimOffspring"),sQuery(id+"F0.wireOp",EDGE,"E17.trimOffspring"),sQuery(id+"F0.wireOp",EDGE,"E18.trimOffspring"),sQuery(id+"F0.wireOp",EDGE,"E19.trimOffspring"),sQuery(id+"F0.wireOp",EDGE,"E20.trimOffspring"),sQuery(id+"F0.wireOp",EDGE,"E21.trimOffspring"),sQuery(id+"F0.wireOp",EDGE,"E22.trimOffspring"),sQuery(id+"F0.wireOp",EDGE,"E23.trimOffspring"),sQuery(id+"F0.wireOp",EDGE,"E24.trimOffspring"),sQuery(id+"F0.wireOp",EDGE,"E25.trimOffspring"),sQuery(id+"F0.wireOp",EDGE,"E26.trimOffspring"),sQuery(id+"F0.wireOp",EDGE,"E27.trimOffspring"),sQuery(id+"F0.wireOp",EDGE,"E28.trimOffspring"),sQuery(id+"F0.wireOp",EDGE,"E29.trimOffspring"),sQuery(id+"F0.wireOp",EDGE,"E30.trimOffspring"),sQuery(id+"F0.wireOp",EDGE,"E31.trimOffspring"),sQuery(id+"F0.wireOp",EDGE,"E32.trimOffspring"),sQuery(id+"F0.wireOp",EDGE,"E33.trimOffspring"),sQuery(id+"F0.wireOp",EDGE,"E34.trimOffspring"),sQuery(id+"F0.wireOp",EDGE,"E35.trimOffspring"),sQuery(id+"F0.wireOp",EDGE,"E36.trimOffspring"),sQuery(id+"F0.wireOp",EDGE,"E37.trimOffspring"),sQuery(id+"F0.wireOp",EDGE,"E38.trimOffspring"),sQuery(id+"F0.wireOp",EDGE,"E39.trimOffspring"),sQuery(id+"F0.wireOp",EDGE,"E40.trimOffspring"),sQuery(id+"F0.wireOp",EDGE,"E41.trimOffspring"),sQuery(id+"F0.wireOp",EDGE,"E42.trimOffspring"),sQuery(id+"F0.wireOp",EDGE,"E43.trimOffspring"),sQuery(id+"F0.wireOp",EDGE,"E44.trimOffspring")])],"isStart":false});
            var sketch = newSketch(context, id + "F2", { "sketchPlane" : qUnion([Q0])});
            skCircle(sketch, "E45", {"center": v(0, 0) * mm, "radius": 11.43 * mm});
            skSolve(sketch);
        }
        {
            var Q0;
            Q0=makeQuery(id+"F2.imprint","IMPRINT",FACE,{"disambiguationData":[TD([[makeQuery(id+"F2.imprint","IMPRINT",EDGE,{"derivedFrom":sQuery(id+"F2.wireOp",EDGE,"E45")}),1.0]])]});
            extrude(context, id + "F3", {"entities" : qUnion([Q0]), "operationType" : NewBodyOperationType.ADD, "depth" : 7.37 * mm});
        }
        {
            var Q0;
            Q0=makeQuery(id+"F3.opExtrude","CAP_FACE",FACE,{"disambiguationData":[OSD([sQuery(id+"F2.wireOp",EDGE,"E45")])],"isStart":false});
            var sketch = newSketch(context, id + "F4", { "sketchPlane" : qUnion([Q0])});
            skPoint(sketch, "E46.0.midPoint", {"position": v(1.2, 0.57) * mm});
            skCircle(sketch, "E47.cCircle", {"center": v(0, 0) * mm, "radius": 5.59 * mm, "construction": true});
            skLineSegment(sketch, "E47.0", {"start": v(2.87, 4.8) * mm, "end": v(5.59, -0.1) * mm});
            skLineSegment(sketch, "E47.1", {"start": v(5.59, -0.1) * mm, "end": v(2.71, -4.89) * mm});
            skLineSegment(sketch, "E47.2", {"start": v(2.71, -4.89) * mm, "end": v(-2.87, -4.8) * mm});
            skLineSegment(sketch, "E47.3", {"start": v(-2.87, -4.8) * mm, "end": v(-5.59, 0.1) * mm});
            skLineSegment(sketch, "E47.4", {"start": v(-5.59, 0.1) * mm, "end": v(-2.71, 4.89) * mm});
            skLineSegment(sketch, "E47.5", {"start": v(-2.71, 4.89) * mm, "end": v(2.87, 4.8) * mm});
            skSolve(sketch);
        }
        {
            var Q0;
            Q0=makeQuery(id+"F4.imprint","IMPRINT",FACE,{"disambiguationData":[TD([[makeQuery(id+"F4.imprint","IMPRINT",EDGE,{"derivedFrom":sQuery(id+"F4.wireOp",EDGE,"E47.0")}),-1.0]])]});
            extrude(context, id + "F5", {"entities" : qUnion([Q0]), "operationType" : NewBodyOperationType.REMOVE, "oppositeDirection" : true, "depth" : 130.8 * mm});
        }
    });
